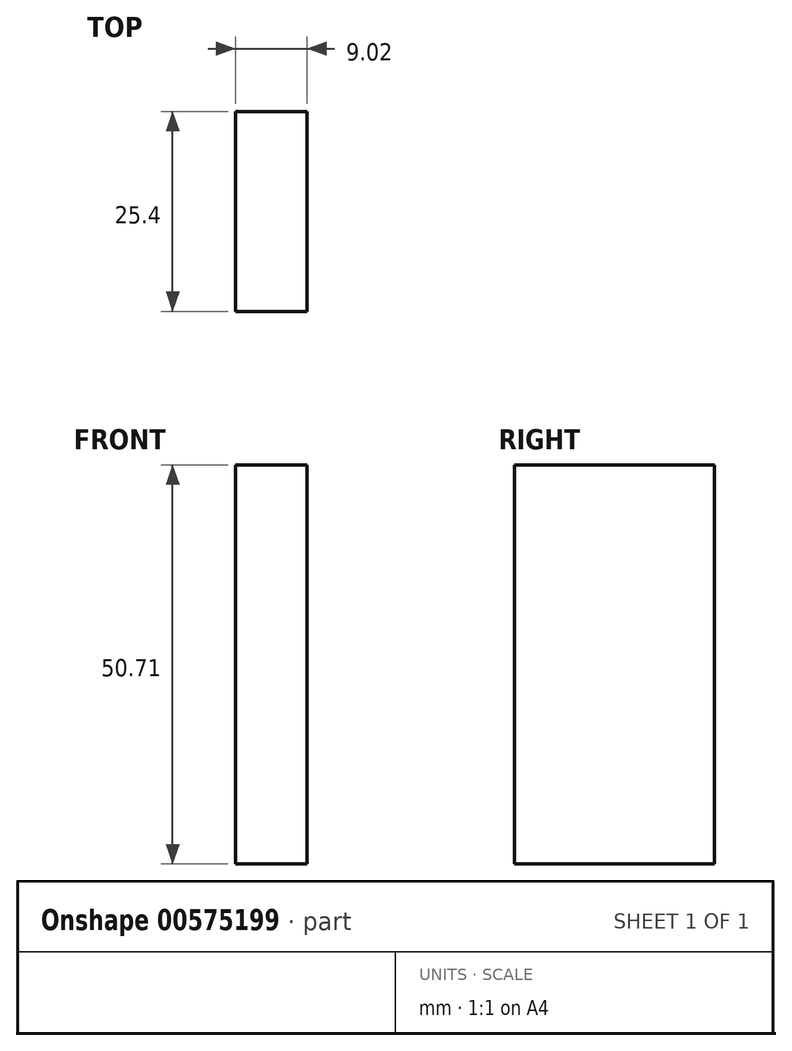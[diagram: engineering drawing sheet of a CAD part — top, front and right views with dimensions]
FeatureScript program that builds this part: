
annotation { "Feature Type Name" : "Feature", "Feature Type Description" : "" }
export const myFeature = defineFeature(function(context is Context, id is Id, definition is map)
    precondition{}
    {
        {
            var Q0;
            Q0=qCreatedBy(makeId("Front.planeOp"),FACE);
            var sketch = newSketch(context, id + "F0", { "sketchPlane" : qUnion([Q0])});
            skLineSegment(sketch, "E0.bottom", {"start": v(-62.67, 35.48) * mm, "end": v(-53.65, 35.48) * mm});
            skLineSegment(sketch, "E0.top", {"start": v(-62.67, -15.23) * mm, "end": v(-53.65, -15.23) * mm});
            skLineSegment(sketch, "E0.left", {"start": v(-62.67, 35.48) * mm, "end": v(-62.67, -15.23) * mm});
            skLineSegment(sketch, "E0.right", {"start": v(-53.65, 35.48) * mm, "end": v(-53.65, -15.23) * mm});
            skLineSegment(sketch, "E1", {"start": v(-52.95, 37.03) * mm, "end": v(-36.23, 42.4) * mm});
            skLineSegment(sketch, "E2", {"start": v(-36.23, 42.4) * mm, "end": v(-52.83, -16.74) * mm});
            skLineSegment(sketch, "E3", {"start": v(-52.83, -16.74) * mm, "end": v(-36.83, -12.04) * mm});
            skLineSegment(sketch, "E4", {"start": v(-36.83, -12.04) * mm, "end": v(-74.89, -131.37) * mm});
            skSolve(sketch);
        }
        {
            var Q0;
            Q0 = qSketchRegion(id + "F0", true);
            extrude(context, id + "F1", {"entities" : qUnion([Q0]), "depth" : 25.4 * mm, "offsetDistance" : 25.4 * mm});
        }
    });
